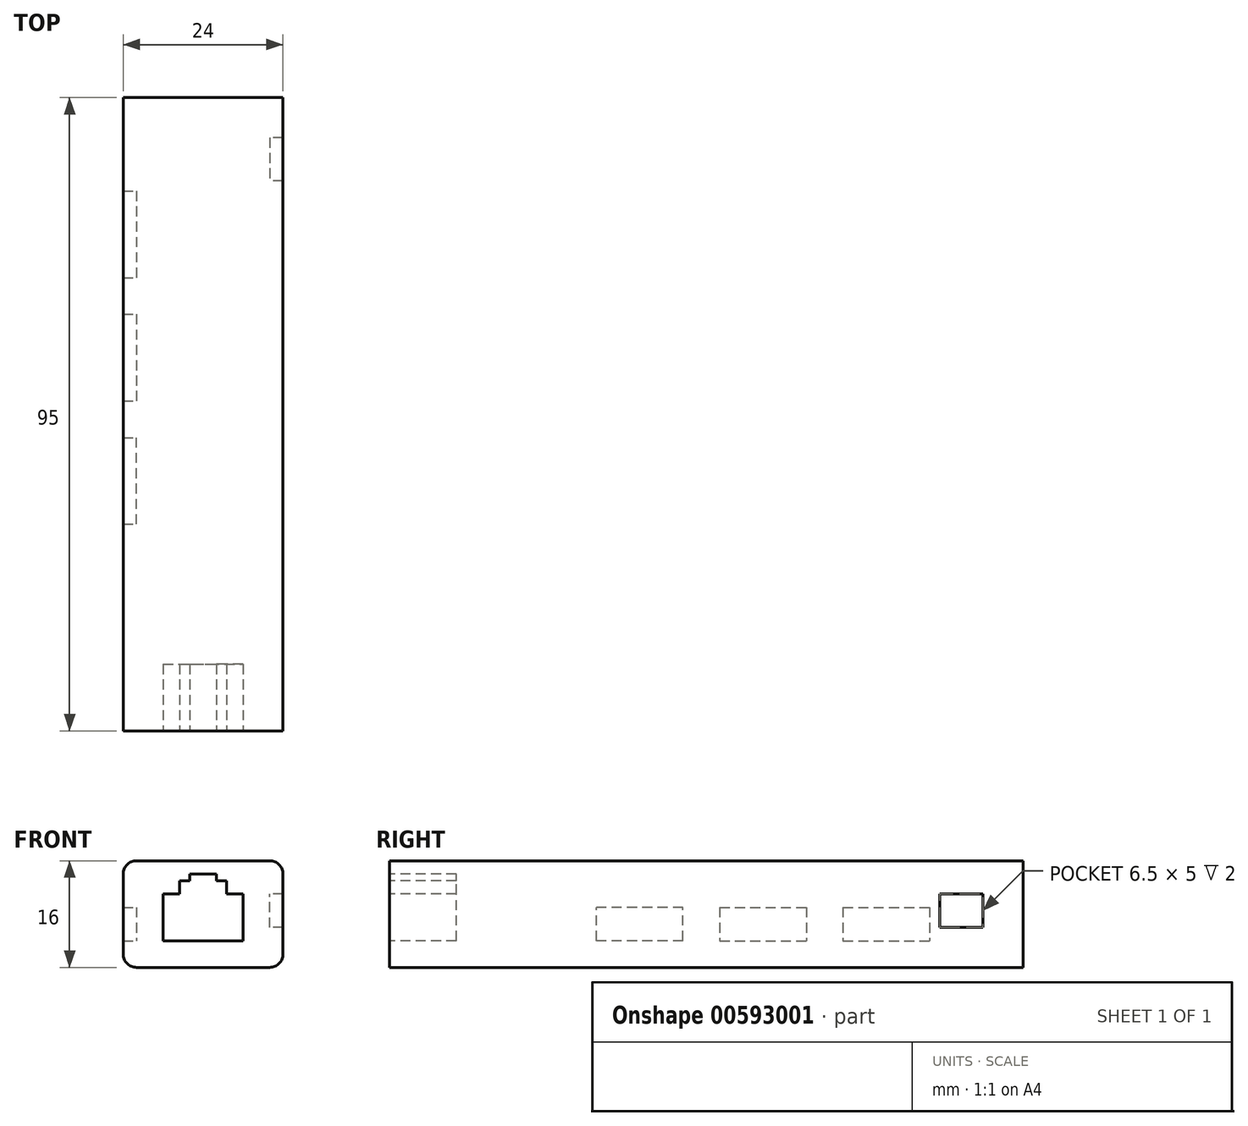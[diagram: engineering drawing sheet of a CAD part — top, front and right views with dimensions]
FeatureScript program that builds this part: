
annotation { "Feature Type Name" : "Feature", "Feature Type Description" : "" }
export const myFeature = defineFeature(function(context is Context, id is Id, definition is map)
    precondition{}
    {
        {
            var Q0;
            Q0=qCreatedBy(makeId("Front.planeOp"),FACE);
            var sketch = newSketch(context, id + "F0", { "sketchPlane" : qUnion([Q0])});
            skLineSegment(sketch, "E0.bottom", {"start": v(10, -8) * mm, "end": v(-10, -8) * mm});
            skLineSegment(sketch, "E0.top", {"start": v(10, 8) * mm, "end": v(-10, 8) * mm});
            skLineSegment(sketch, "E0.left", {"start": v(12, -6) * mm, "end": v(12, 6) * mm});
            skLineSegment(sketch, "E0.right", {"start": v(-12, -6) * mm, "end": v(-12, 6) * mm});
            skPoint(sketch, "E0.middle", {"position": v(0, 0) * mm});
            skPoint(sketch, "E1.visualSharp", {"position": v(-12, 8) * mm});
            skArc(sketch, "E1.filletArc", {"start": v(-10, 8) * mm, "mid": v(-11.41, 7.41) * mm, "end": v(-12, 6) * mm});
            skPoint(sketch, "E2.visualSharp", {"position": v(12, 8) * mm});
            skArc(sketch, "E2.filletArc", {"start": v(12, 6) * mm, "mid": v(11.41, 7.41) * mm, "end": v(10, 8) * mm});
            skPoint(sketch, "E3.visualSharp", {"position": v(12, -8) * mm});
            skArc(sketch, "E3.filletArc", {"start": v(10, -8) * mm, "mid": v(11.41, -7.41) * mm, "end": v(12, -6) * mm});
            skPoint(sketch, "E4.visualSharp", {"position": v(-12, -8) * mm});
            skArc(sketch, "E4.filletArc", {"start": v(-12, -6) * mm, "mid": v(-11.41, -7.41) * mm, "end": v(-10, -8) * mm});
            skLineSegment(sketch, "E5", {"start": v(-2, 6) * mm, "end": v(2, 6) * mm});
            skLineSegment(sketch, "E6", {"start": v(0, -8) * mm, "end": v(0, -4) * mm, "construction": true});
            skLineSegment(sketch, "E7", {"start": v(-6, -4) * mm, "end": v(6, -4) * mm});
            skLineSegment(sketch, "E8", {"start": v(0, 8) * mm, "end": v(0, 6) * mm, "construction": true});
            skLineSegment(sketch, "E9", {"start": v(-6, -4) * mm, "end": v(-6, 3) * mm});
            skLineSegment(sketch, "E10", {"start": v(-6, 3) * mm, "end": v(-3.5, 3) * mm});
            skLineSegment(sketch, "E11", {"start": v(-3.5, 3) * mm, "end": v(-3.5, 5) * mm});
            skLineSegment(sketch, "E12", {"start": v(-3.5, 5) * mm, "end": v(-2, 5) * mm});
            skLineSegment(sketch, "E13", {"start": v(-2, 5) * mm, "end": v(-2, 6) * mm});
            skLineSegment(sketch, "E14.MirrorCS", {"start": v(2, 5) * mm, "end": v(2, 6) * mm});
            skLineSegment(sketch, "E15.MirrorCS", {"start": v(3.5, 5) * mm, "end": v(2, 5) * mm});
            skLineSegment(sketch, "E16.MirrorCS", {"start": v(3.5, 3) * mm, "end": v(3.5, 5) * mm});
            skLineSegment(sketch, "E17.MirrorCS", {"start": v(6, 3) * mm, "end": v(3.5, 3) * mm});
            skLineSegment(sketch, "E18.MirrorCS", {"start": v(6, -4) * mm, "end": v(6, 3) * mm});
            skSolve(sketch);
        }
        {
            var Q0;
            Q0=makeQuery(id+"F0.imprint","IMPRINT",FACE,{"disambiguationData":[TD([[makeQuery(id+"F0.imprint","IMPRINT",EDGE,{"derivedFrom":sQuery(id+"F0.wireOp",EDGE,"E0.bottom")}),-1.0]])]});
            var Q1;
            Q1=makeQuery(id+"F0.imprint","IMPRINT",FACE,{"disambiguationData":[TD([[makeQuery(id+"F0.imprint","IMPRINT",EDGE,{"derivedFrom":sQuery(id+"F0.wireOp",EDGE,"E5")}),-1.0]])]});
            extrude(context, id + "F1", {"entities" : qUnion([Q0, Q1]), "oppositeDirection" : true, "depth" : 95 * mm, "offsetDistance" : 25 * mm});
        }
        {
            var Q0;
            Q0=makeQuery(id+"F0.imprint","IMPRINT",FACE,{"disambiguationData":[TD([[makeQuery(id+"F0.imprint","IMPRINT",EDGE,{"derivedFrom":sQuery(id+"F0.wireOp",EDGE,"E5")}),-1.0]])]});
            extrude(context, id + "F2", {"entities" : qUnion([Q0]), "operationType" : NewBodyOperationType.REMOVE, "oppositeDirection" : true, "depth" : 10 * mm, "offsetDistance" : 25 * mm});
        }
        {
            var Q0;
            Q0=qCreatedBy(makeId("Right.planeOp"),FACE);
            var sketch = newSketch(context, id + "F3", { "sketchPlane" : qUnion([Q0])});
            skLineSegment(sketch, "E19.bottom", {"start": v(89, -2) * mm, "end": v(82.5, -2) * mm});
            skLineSegment(sketch, "E19.top", {"start": v(89, 3) * mm, "end": v(82.5, 3) * mm});
            skLineSegment(sketch, "E19.left", {"start": v(89, -2) * mm, "end": v(89, 3) * mm});
            skLineSegment(sketch, "E19.right", {"start": v(82.5, -2) * mm, "end": v(82.5, 3) * mm});
            skPoint(sketch, "E19.middle", {"position": v(85.75, 0.5) * mm});
            skLineSegment(sketch, "E20.bottom", {"start": v(81, -4) * mm, "end": v(68, -4) * mm});
            skLineSegment(sketch, "E20.top", {"start": v(81, 1) * mm, "end": v(68, 1) * mm});
            skLineSegment(sketch, "E20.left", {"start": v(81, -4) * mm, "end": v(81, 1) * mm});
            skLineSegment(sketch, "E20.right", {"start": v(68, -4) * mm, "end": v(68, 1) * mm});
            skPoint(sketch, "E20.middle", {"position": v(74.5, -1.5) * mm});
            skLineSegment(sketch, "E21.bottom", {"start": v(62.5, -4) * mm, "end": v(49.5, -4) * mm});
            skLineSegment(sketch, "E21.top", {"start": v(62.5, 1) * mm, "end": v(49.5, 1) * mm});
            skLineSegment(sketch, "E21.left", {"start": v(62.5, -4) * mm, "end": v(62.5, 1) * mm});
            skLineSegment(sketch, "E21.right", {"start": v(49.5, -4) * mm, "end": v(49.5, 1) * mm});
            skPoint(sketch, "E21.middle", {"position": v(56, -1.5) * mm});
            skLineSegment(sketch, "E22.bottom", {"start": v(31, 1) * mm, "end": v(44, 1) * mm});
            skLineSegment(sketch, "E22.top", {"start": v(31, -4) * mm, "end": v(44, -4) * mm});
            skLineSegment(sketch, "E22.left", {"start": v(31, 1) * mm, "end": v(31, -4) * mm});
            skLineSegment(sketch, "E22.right", {"start": v(44, 1) * mm, "end": v(44, -4) * mm});
            skPoint(sketch, "E22.middle", {"position": v(37.5, -1.5) * mm});
            skSolve(sketch);
        }
        {
            var Q0;
            Q0=makeQuery(id+"F3.imprint","IMPRINT",FACE,{"disambiguationData":[TD([[makeQuery(id+"F3.imprint","IMPRINT",EDGE,{"derivedFrom":sQuery(id+"F3.wireOp",EDGE,"E19.bottom")}),-1.0]])]});
            var Q1;
            Q1=makeQuery(id+"F1.opExtrude","SWEPT_FACE",FACE,{"disambiguationData":[OSD([sQuery(id+"F0.wireOp",EDGE,"E0.left")])]});
            extrude(context, id + "F4", {"entities" : qUnion([Q0]), "operationType" : NewBodyOperationType.REMOVE, "endBound" : BoundingType.UP_TO_SURFACE, "depth" : 25 * mm, "endBoundEntityFace" : qUnion([Q1]), "offsetDistance" : 25 * mm, "hasSecondDirection" : true, "secondDirectionOppositeDirection" : false, "secondDirectionDepth" : 10 * mm});
        }
        {
            var Q0;
            Q0=makeQuery(id+"F3.imprint","IMPRINT",FACE,{"disambiguationData":[TD([[makeQuery(id+"F3.imprint","IMPRINT",EDGE,{"derivedFrom":sQuery(id+"F3.wireOp",EDGE,"E20.bottom")}),-1.0]])]});
            var Q1;
            Q1=makeQuery(id+"F3.imprint","IMPRINT",FACE,{"disambiguationData":[TD([[makeQuery(id+"F3.imprint","IMPRINT",EDGE,{"derivedFrom":sQuery(id+"F3.wireOp",EDGE,"E21.bottom")}),-1.0]])]});
            var Q2;
            Q2=makeQuery(id+"F3.imprint","IMPRINT",FACE,{"disambiguationData":[TD([[makeQuery(id+"F3.imprint","IMPRINT",EDGE,{"derivedFrom":sQuery(id+"F3.wireOp",EDGE,"E22.bottom")}),-1.0]])]});
            var Q3;
            Q3=makeQuery(id+"F1.opExtrude","SWEPT_FACE",FACE,{"disambiguationData":[OSD([sQuery(id+"F0.wireOp",EDGE,"E0.right")])]});
            extrude(context, id + "F5", {"entities" : qUnion([Q0, Q1, Q2]), "operationType" : NewBodyOperationType.REMOVE, "endBound" : BoundingType.UP_TO_SURFACE, "oppositeDirection" : true, "depth" : 25 * mm, "endBoundEntityFace" : qUnion([Q3]), "offsetDistance" : 25 * mm, "hasSecondDirection" : true, "secondDirectionOppositeDirection" : true, "secondDirectionDepth" : 10 * mm});
        }
    });
